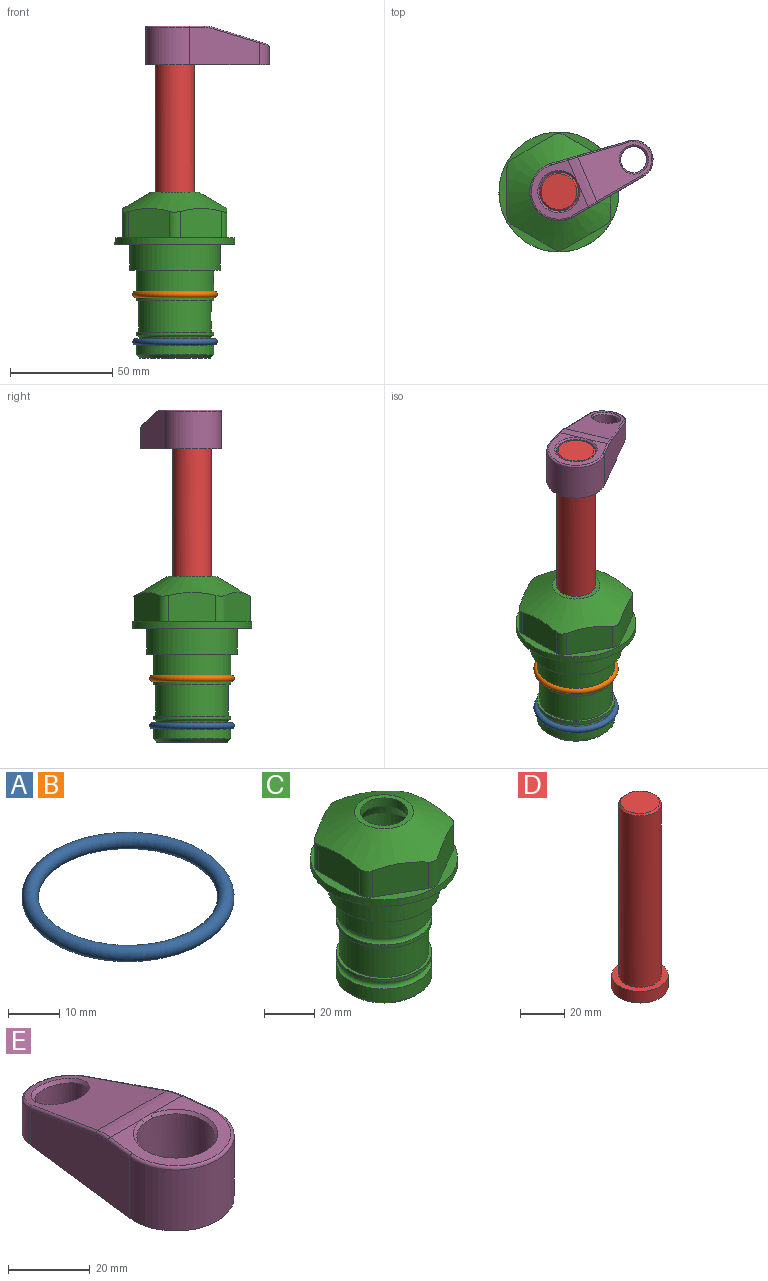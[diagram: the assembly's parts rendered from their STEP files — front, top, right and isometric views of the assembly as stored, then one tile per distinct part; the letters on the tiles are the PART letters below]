
ASSEMBLY  parts=5 mates=4
PART A: 1 faces, bbox 44.7x44.7x3.2 mm
  f0: torus R=19.05mm, axis (0,0,1), area 1193.9mm2
PART B: same geometry as A
PART C: 36 faces, bbox 58.7x58.7x81 mm
  f0: cylinder r=17.78mm len=35.56mm, axis (0,0,1), area 1670.8mm2, adj f23,f24,f31
  f1: cylinder r=19.05mm len=38.1mm, axis (0,0,1), area 1191.9mm2, adj f26,f27,f30
  f2: plane 58.66x58.66mm, normal (0,0,-1), area 1150.6mm2, adj f3,f28
  f3: cylinder r=29.33mm len=58.66mm, axis (0,0,-1), area 585.1mm2, adj f2,f4
  f4: plane 58.66x58.66mm, normal (0,0,1), area 475.9mm2, adj f3,f5,f6,f7,f8,f9,f10,f11
  f5: plane 20.32x14.34mm, normal (-0.5,0.87,0), area 324.4mm2, adj f4,f15,f16,f17
  f6: plane 20.32x14.34mm, normal (0.5,0.87,0), area 324.4mm2, adj f4,f14,f15,f17
  f7: plane 23.48x14.34mm, normal (1,0,0), area 324.4mm2, adj f4,f13,f14,f17
  f8: plane 20.32x14.34mm, normal (0.5,-0.87,0), area 324.4mm2, adj f4,f12,f13,f17
  f9: plane 20.32x14.34mm, normal (-0.5,-0.87,0), area 324.4mm2, adj f4,f11,f12,f17
  f10: plane 23.48x14.34mm, normal (-1,0,0), area 324.4mm2, adj f4,f11,f16,f17
  f11: cylinder r=5.08mm len=12.85mm, axis (0,0,-1), area 67.2mm2, adj f4,f9,f10,f17
  f12: cylinder r=5.08mm len=12.85mm, axis (0,0,-1), area 67.2mm2, adj f4,f8,f9,f17
  f13: cylinder r=5.08mm len=12.85mm, axis (0,0,-1), area 67.2mm2, adj f4,f7,f8,f17
  f14: cylinder r=5.08mm len=12.85mm, axis (0,0,-1), area 67.2mm2, adj f4,f6,f7,f17
  f15: cylinder r=5.08mm len=12.85mm, axis (0,0,-1), area 67.2mm2, adj f4,f5,f6,f17
  f16: cylinder r=5.08mm len=12.85mm, axis (0,0,-1), area 67.2mm2, adj f4,f5,f10,f17
  f17: cone r=11.73mm half-angle=60deg, axis (0,0,-1), area 2071.8mm2, adj f5,f6,f7,f8,f9,f10,f11,f12
  f18: plane 23.46x23.46mm, normal (0,0,1), area 147.4mm2, adj f17,f35
  f19: plane 34.93x34.93mm, normal (0,0,-1), area 958mm2, adj f29
  f20: cylinder r=19.05mm len=38.1mm, axis (0,0,1), area 760.1mm2, adj f21,f29
  f21: torus R=19.05mm, axis (0,0,1), area 565.3mm2, adj f20,f22
  f22: cylinder r=19.05mm len=38.1mm, axis (0,0,1), area 190mm2, adj f21,f23
  f23: plane 38.1x38.1mm, normal (0,0,1), area 146.9mm2, adj f0,f22
  f24: plane 38.1x38.1mm, normal (0,0,-1), area 146.9mm2, adj f0,f25
  f25: cylinder r=19.05mm len=38.1mm, axis (0,0,1), area 190mm2, adj f24,f26
  f26: torus R=19.05mm, axis (0,0,1), area 565.3mm2, adj f1,f25
  f27: plane 44.45x44.45mm, normal (0,0,-1), area 411.7mm2, adj f1,f28
  f28: cylinder r=22.23mm len=44.45mm, axis (0,0,1), area 1773.5mm2, adj f2,f27
  f29: cone r=19.05mm half-angle=45deg, axis (0,0,1), area 257.5mm2, adj f19,f20
  f30: cylinder r=3.17mm len=6.75mm, axis (-1,0,0), area 128mm2, adj f1,f33
  f31: cylinder r=3.17mm len=6.35mm, axis (-1,0,0), area 102.5mm2, adj f0,f33
  f32: plane 25.4x25.4mm, normal (0,0,1), area 506.7mm2, adj f33
  f33: cylinder r=12.7mm len=66.42mm, axis (0,0,-1), area 5236.2mm2, adj f30,f31,f32,f34
  f34: cone r=9.53mm half-angle=30deg, axis (0,0,-1), area 443.4mm2, adj f33,f35
  f35: cylinder r=9.53mm len=19.05mm, axis (0,0,-1), area 240.9mm2, adj f18,f34
PART D: 6 faces, bbox 25.4x25.4x101.6 mm
  f0: plane 17.46x17.46mm, normal (0,0,1), area 239.5mm2, adj f5
  f1: plane 25.4x25.4mm, normal (0,0,-1), area 506.7mm2, adj f2
  f2: cylinder r=12.7mm len=25.4mm, axis (0,0,1), area 506.7mm2, adj f1,f3
  f3: plane 25.4x25.4mm, normal (0,0,1), area 221.7mm2, adj f2,f4
  f4: cylinder r=9.53mm len=94.46mm, axis (0,0,1), area 5653mm2, adj f3,f5
  f5: cone r=8.73mm half-angle=45deg, axis (0,0,-1), area 64.4mm2, adj f0,f4
PART E: 31 faces, bbox 31.7x65.5x19.8 mm
  f0: plane 39.12x18.26mm, normal (0.99,0.12,0), area 612.2mm2, adj f1,f4,f7,f11,f13,f15
  f1: cylinder r=9.53mm len=18.91mm, axis (0,0,-1), area 296.1mm2, adj f0,f2,f7,f17
  f2: plane 39.12x18.26mm, normal (-0.99,0.12,0), area 612.2mm2, adj f1,f4,f7,f12,f14,f16
  f3: cylinder r=6.35mm len=12.7mm, axis (0,0,-1), area 362.4mm2, adj f7,f18
  f4: cylinder r=14.29mm len=28.58mm, axis (0,0,-1), area 882.2mm2, adj f0,f2,f7,f10
  f5: cylinder r=9.53mm len=19.05mm, axis (0,0,-1), area 1092.6mm2, adj f7,f19,f20
  f6: plane 26.99x23.69mm, normal (0,0,1), area 216.2mm2, adj f9,f10,f11,f12,f19
  f7: plane 63.5x28.58mm, normal (0,0,-1), area 661.8mm2, adj f0,f1,f2,f3,f4,f5,f22,f23
  f8: plane 33.52x23.6mm, normal (0,0.26,0.97), area 486mm2, adj f9,f15,f16,f17,f18
  f9: cylinder r=19.05mm len=24.72mm, axis (1,0,0), area 120.4mm2, adj f6,f8,f13,f14,f20
  f10: torus R=13.49mm, axis (0,0,1), area 59mm2, adj f4,f6,f11,f12
  f11: cylinder r=0.79mm len=8.67mm, axis (0.12,-0.99,0), area 10.8mm2, adj f0,f6,f10,f13
  f12: cylinder r=0.79mm len=8.67mm, axis (0.12,0.99,0), area 10.8mm2, adj f2,f6,f10,f14
  f13: bspline ~4.95x1.42mm, area 6.1mm2, adj f0,f9,f11,f15
  f14: bspline ~4.95x1.42mm, area 6.1mm2, adj f2,f9,f12,f16
  f15: cylinder r=0.79mm len=25.95mm, axis (0.12,-0.96,0.26), area 32.9mm2, adj f0,f8,f13,f17
  f16: cylinder r=0.79mm len=25.95mm, axis (0.12,0.96,-0.26), area 32.9mm2, adj f2,f8,f14,f17
  f17: bspline ~18.91x8.38mm, area 30mm2, adj f1,f8,f15,f16
  f18: bspline ~14.29x14.29mm, area 48.3mm2, adj f3,f8
  f19: cone r=9.53mm half-angle=45deg, axis (0,0,1), area 66.5mm2, adj f5,f6,f20
  f20: bspline ~3.22x0.96mm, area 3.5mm2, adj f5,f9,f19
  f21: plane 2.75x2.72mm, normal (0,0,-1), area 2.9mm2, adj f23,f25,f28
  f22: plane 23.05x15.88mm, normal (-0.99,-0.12,0), area 323.6mm2, adj f7,f25,f26,f27,f28,f29
  f23: plane 23.05x15.88mm, normal (0.99,-0.12,0), area 323.6mm2, adj f7,f21,f25,f27,f28,f30
  f24: cylinder r=9.53mm len=10.69mm, axis (0,0,-1), area 114.7mm2, adj f7,f27,f29,f30
  f25: cylinder r=12.7mm len=20.59mm, axis (0,0,-1), area 381.1mm2, adj f7,f21,f22,f23,f26,f28
  f26: plane 2.75x2.72mm, normal (0,0,-1), area 2.9mm2, adj f22,f25,f28
  f27: plane 19.72x18.37mm, normal (0,-0.26,-0.97), area 291.8mm2, adj f22,f23,f24,f28,f29,f30
  f28: cylinder r=15.88mm len=19.92mm, axis (1,0,0), area 54.8mm2, adj f21,f22,f23,f25,f26,f27
  f29: cylinder r=1.59mm len=11mm, axis (0,0,-1), area 34.7mm2, adj f7,f22,f24,f27
  f30: cylinder r=1.59mm len=11mm, axis (0,0,-1), area 34.7mm2, adj f7,f23,f24,f27
PLACE A t=(0,0,-23.18)mm
PLACE B at identity
PLACE C at identity fixed
PLACE D rot(axis=(0,0,-1),66.8deg) t=(0,0,42.4)mm
PLACE E rot(axis=(0,0,-1),66.8deg) t=(0,0,43.19)mm
MATE fastened A.f0 <-> C.f0  axis (0,0,1) through (0,0,-47.69)mm
MATE cylindrical D.f2 <-> C.f0  axis (0,0,-1) through (0,0,4.3)mm
MATE fastened B.f0 <-> C.f0  axis (0,0,1) through (0,0,-24.51)mm
MATE fastened D.f2 <-> E.f4  axis (0,0,1) through (0,0,105.9)mm
